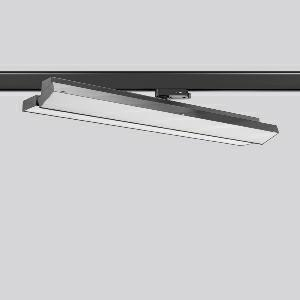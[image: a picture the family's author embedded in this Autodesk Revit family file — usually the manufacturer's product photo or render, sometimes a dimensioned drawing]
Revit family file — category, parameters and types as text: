
# Revit family: tx-move_742164_003_76_4a04
name_source: partatom
category: Lighting Fixtures
units: mm (PartAtom-declared; Revit-internal decimal feet)

## family parameters
Cut with Voids When Loaded = No
Host = Face
Light Source = No
Part Type = Normal
Room Calculation Point = No
Round Connector Dimension = Use Diameter
Shared = No

## types (1)
- MultiLumen 1 (1 x LED Modul 830, 2450 lm, 3000)
    Apparent Load = 41 VA
    CIE Flux Codes = 47 79 96 100 100
    Color Rendering = 80
    Color Temperature = 3000
    Default Elevation = 1800 mm
    Description = Series: TX-MOVE
Multifunctional surface-mounted spotlight for area lighting. Very flat design. Housing: sheet steel, powder-coated. Rotation range: 356°. Swivel range: 90°. Consistent alignment possible with visible tilt scale. High-efficiency LED units with flush-mounted opal diffuser made of non-yellowing PMMA. Symmetrical wide beam light emission. With adapter for RZB 3-circuit DALI tracks. Suitable for Track on ceiling. MultiLumen: Luminous flux adjustable in 3 steps. Factory setting is the highest luminous flux. Environmentally friendly and resource-saving due to replaceable and recyclable components. 
Colour: deep black, matt (RAL 9005)
Length: 570 mm
Width: 119 mm
Height: 88 mm
Lamp: LED
Socket: without socket
Colour temperature: 3000K
Colour rendering index (CRI): 80
System power: 41 W
Rated luminous flux: 4900 lm
Luminous efficiency: 120 lm/W
System power 2: 57 W
Rated luminous flux 2: 6650 lm
Luminous efficiency 2: 117 lm/W
System power 3: 73 W
Rated luminous flux 3: 8150 lm
Luminous efficiency 3: 112 lm/W
Control gear: Dimmable EVG, DALI
Protection class: I
Type of protection: IP 20
    Height = 75 mm
    Lamp = 1 x LED Modul 830
    Lamp Light Flux = 2450 lm
    Lamp count = 1
    Length = 569 mm
    Lifetime = 50000 h
    Luminous efficacy = 120 lm/W
    Manufacturer = RZB
    ModVariant = No
    Model = 742164.003.76
    Mounting Place = Ceiling
    Mounting Type = Surface mounted
    Number of Poles = 1
    OnlyDefault = Yes
    Power Factor = 1
    Product Name = TX-MOVE
    Product group = Track mounted projectors
    ProductGroupID = 301
    Protection Class = Protection class I
    Protection Degree = IP 20
    RLX_Detail_Level = 1
    RLX_Emergency_Light_Flux = 0 lm
    RLX_Emergency_Type = 0
    RLX_Emergency_Type_DB = No
    RlxData = <blob elided: 35701 chars, md5=29bfb4cb>
    Socket = socket
    Standby Power = 0 W
    System Light Flux = 4900 lm
    System Power = 41 W
    Type Comments = MultiLumen 1
    Type Image = 742164.003.jpg
    URL = http://relux.com
    VarID = multilumen_1
    Voltage = 0 V
    Weight = 0.00 kg
    Width = 119 mm

## geometry (parser evidence)
native form markers: Blend x4, Sweep x13
no freeform markers — native parametric forms only
